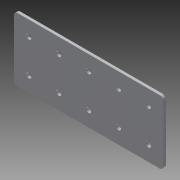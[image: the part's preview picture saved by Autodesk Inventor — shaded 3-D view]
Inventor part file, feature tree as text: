
AUTODESK INVENTOR PART (.ipt)
format: ipt  version: 2014 (Build 180170000, 170)  size: 111,616 bytes
history: native  units: in
note: dims shown in document units (in); Inventor stores cm internally (conversion verified against a paired STEP export)
features: sheet_metal_op x1, fillet x1, sketch x1, other x1
ambient origin geometry x8: Origin, YZ Plane, XZ Plane, XY Plane, X Axis, Y Axis, Z Axis, Center Point
bodies: Solid1 (feature_tree)
feature tree (4):
  sheet_metal_op  "Face1"
  fillet  "Fillet1"  Radius=5.0in
  sketch  "Sketch1"  dims[d1=2.125in d2=1.0625in d3=0.164in d4=0.5in d5=1.9685in d7=1.0in d8=0.3937in d10=1.0in d12=0.5in d13=0.09in d14=0.125in]
  other  "Plate1"
